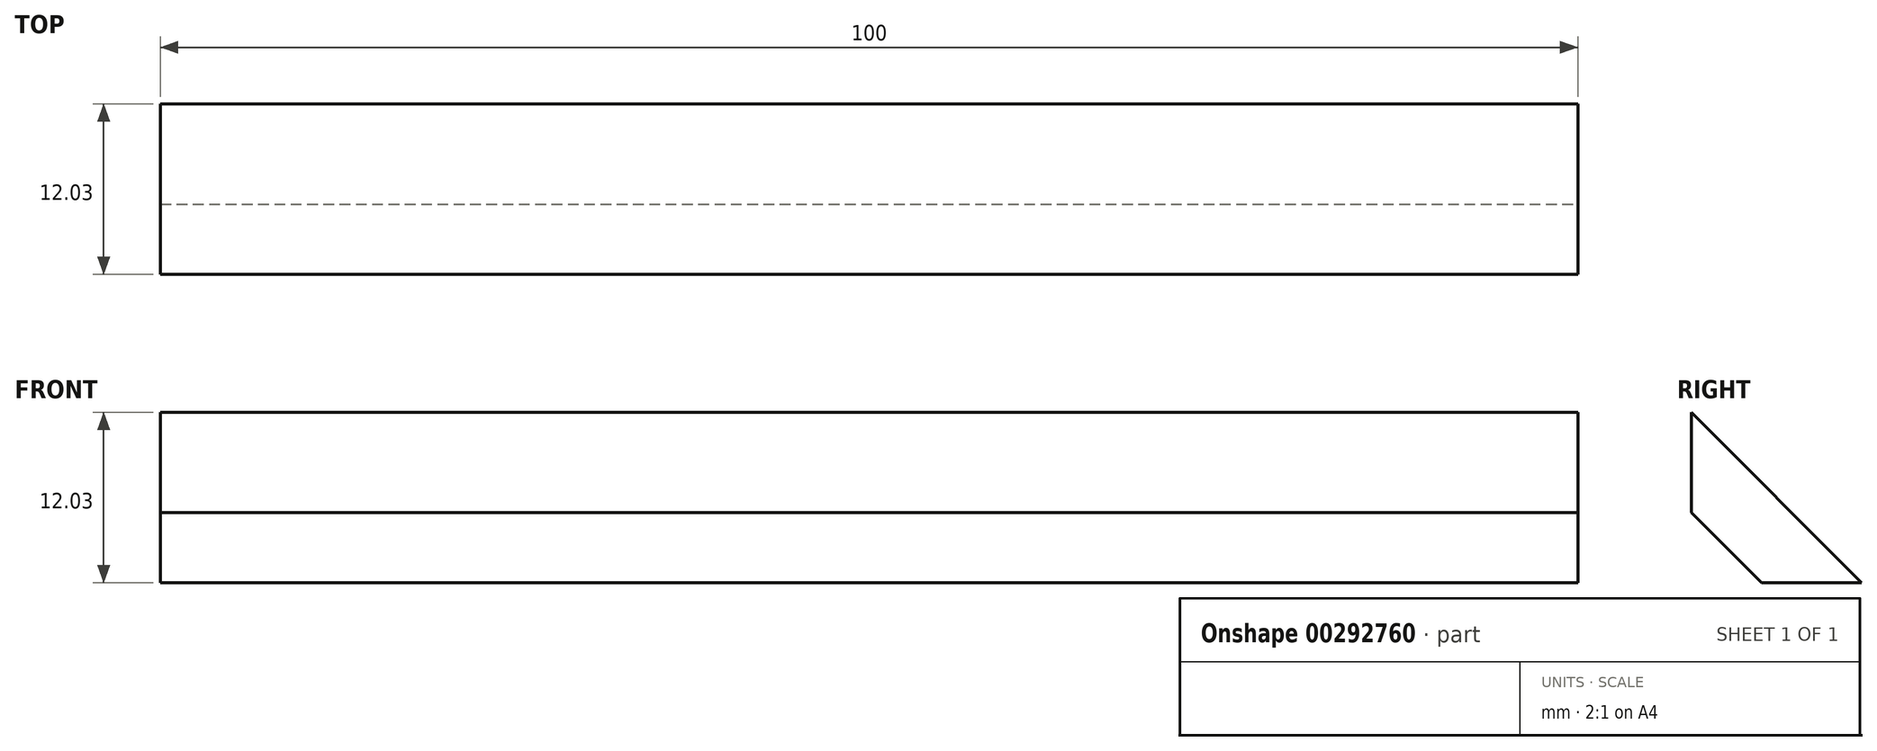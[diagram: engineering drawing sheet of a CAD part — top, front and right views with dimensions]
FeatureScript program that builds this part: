
annotation { "Feature Type Name" : "Feature", "Feature Type Description" : "" }
export const myFeature = defineFeature(function(context is Context, id is Id, definition is map)
    precondition{}
    {
        {
            var Q0;
            Q0=qCreatedBy(makeId("Right.planeOp"),FACE);
            var sketch = newSketch(context, id + "F0", { "sketchPlane" : qUnion([Q0])});
            skLineSegment(sketch, "E0", {"start": v(-4.53, 10.74) * mm, "end": v(7.5, -1.29) * mm});
            skLineSegment(sketch, "E1", {"start": v(-4.53, 10.74) * mm, "end": v(-8.06, 7.2) * mm});
            skLineSegment(sketch, "E2", {"start": v(7.5, -1.29) * mm, "end": v(3.96, -4.82) * mm});
            skLineSegment(sketch, "E3", {"start": v(-8.06, 7.2) * mm, "end": v(3.96, -4.82) * mm});
            skSolve(sketch);
        }
        {
            var Q0;
            Q0=makeQuery(id+"F0.imprint","IMPRINT",FACE,{"disambiguationData":[TD([[makeQuery(id+"F0.imprint","IMPRINT",EDGE,{"derivedFrom":sQuery(id+"F0.wireOp",EDGE,"E0")}),-1.0]])]});
            extrude(context, id + "F1", {"entities" : qUnion([Q0]), "depth" : 100 * mm});
        }
        {
            var Q0;
            Q0=makeQuery(id+"F1.opExtrude","SWEPT_EDGE",EDGE,{"disambiguationData":[OSD([sQuery(id+"F0.wireOp",EDGE,"E1"),sQuery(id+"F0.wireOp",EDGE,"E3")])]});
            var Q1;
            Q1=makeQuery(id+"F1.opExtrude","SWEPT_EDGE",EDGE,{"disambiguationData":[OSD([sQuery(id+"F0.wireOp",EDGE,"E2"),sQuery(id+"F0.wireOp",EDGE,"E3")])]});
            chamfer(context, id + "F2", {"entities" : qUnion([Q0, Q1]), "width" : 5 * mm, "tangentPropagation" : true});
        }
    });
